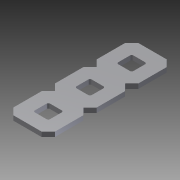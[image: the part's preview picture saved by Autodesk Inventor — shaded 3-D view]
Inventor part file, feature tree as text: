
AUTODESK INVENTOR PART (.ipt)
format: ipt  version: 2014 SP1 (Build 180222100, 222)  size: 489,984 bytes
history: native  units: in
note: dims shown in document units (in); Inventor stores cm internally (conversion verified against a paired STEP export)
features: other x1, imported_body x1, extrude x1, sketch x1
ambient origin geometry x8: Origin, YZ Plane, XZ Plane, XY Plane, X Axis, Y Axis, Z Axis, Center Point
bodies: Body1 (feature_tree)
feature tree (4):
  parser-record x1  (decoder bookkeeping rows leaked as tree rows — omitted from the tree; the rows remain in map.json)
  imported_body  "Base1"
  extrude  "Extrusion1"  Depth=1.0in TaperAngle=0.0deg
  sketch  "Sketch1"  dims[d0=1.5in d1=1.0in d2=0.0in]
